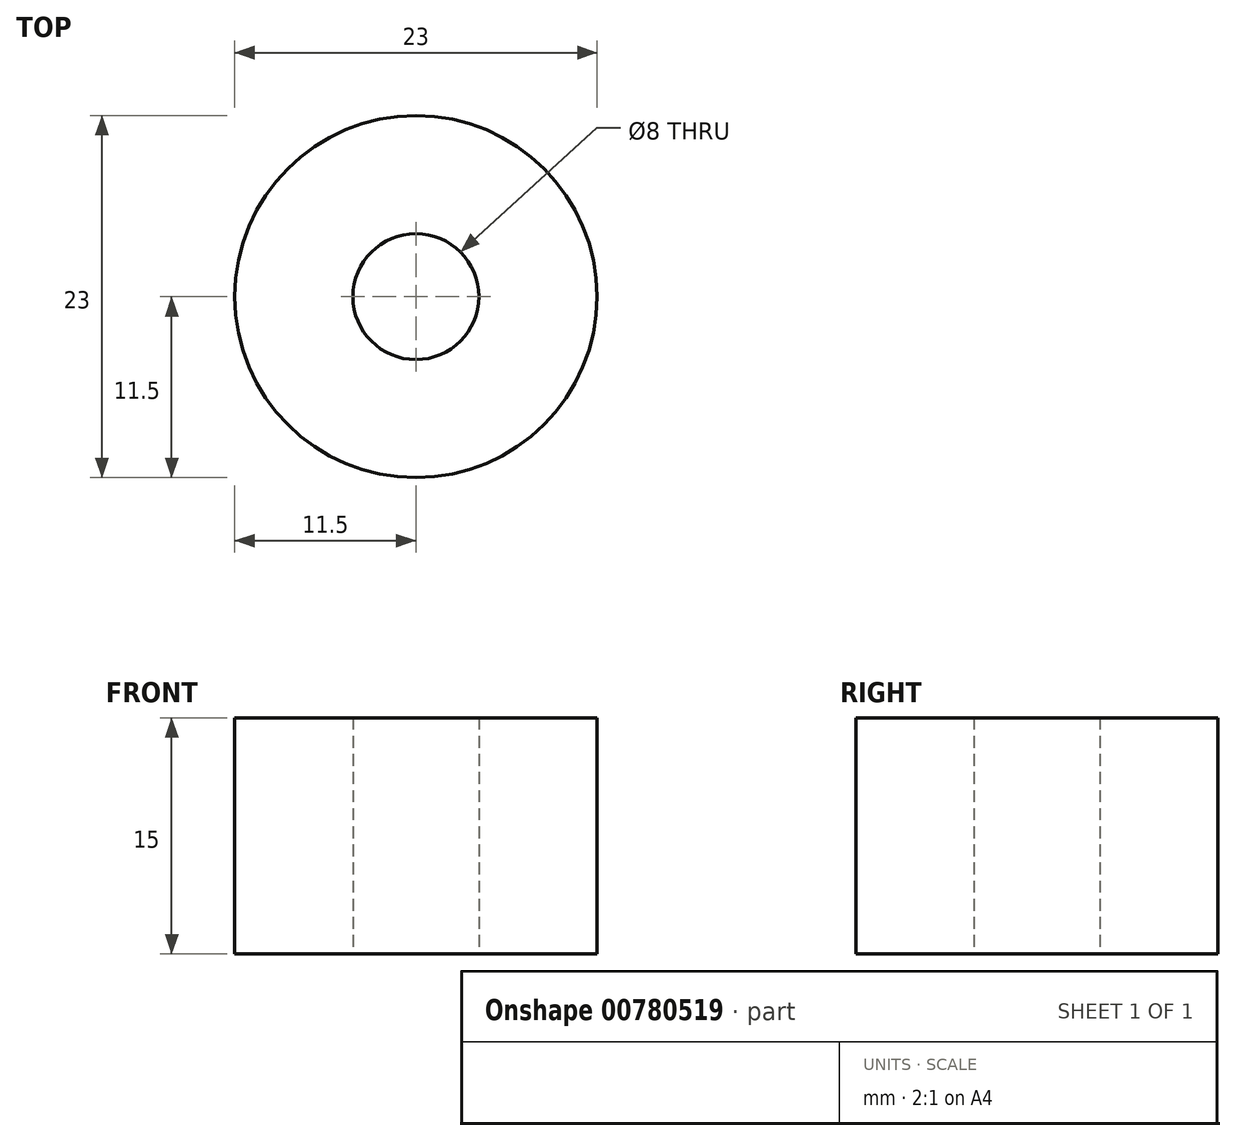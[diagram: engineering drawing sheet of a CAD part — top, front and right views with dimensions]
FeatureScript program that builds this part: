
annotation { "Feature Type Name" : "Feature", "Feature Type Description" : "" }
export const myFeature = defineFeature(function(context is Context, id is Id, definition is map)
    precondition{}
    {
        {
            var Q0;
            Q0=qCreatedBy(makeId("Top.planeOp"),FACE);
            var sketch = newSketch(context, id + "F0", { "sketchPlane" : qUnion([Q0])});
            skCircle(sketch, "E0", {"center": v(0, 0) * mm, "radius": 11.5 * mm});
            skCircle(sketch, "E1", {"center": v(0, 0) * mm, "radius": 4 * mm});
            skSolve(sketch);
        }
        {
            var Q0;
            Q0=makeQuery(id+"F0.imprint","IMPRINT",FACE,{"disambiguationData":[TD([[makeQuery(id+"F0.imprint","IMPRINT",EDGE,{"derivedFrom":sQuery(id+"F0.wireOp",EDGE,"E0")}),1.0]])]});
            extrude(context, id + "F1", {"entities" : qUnion([Q0]), "depth" : 15 * mm, "offsetDistance" : 25 * mm});
        }
    });
